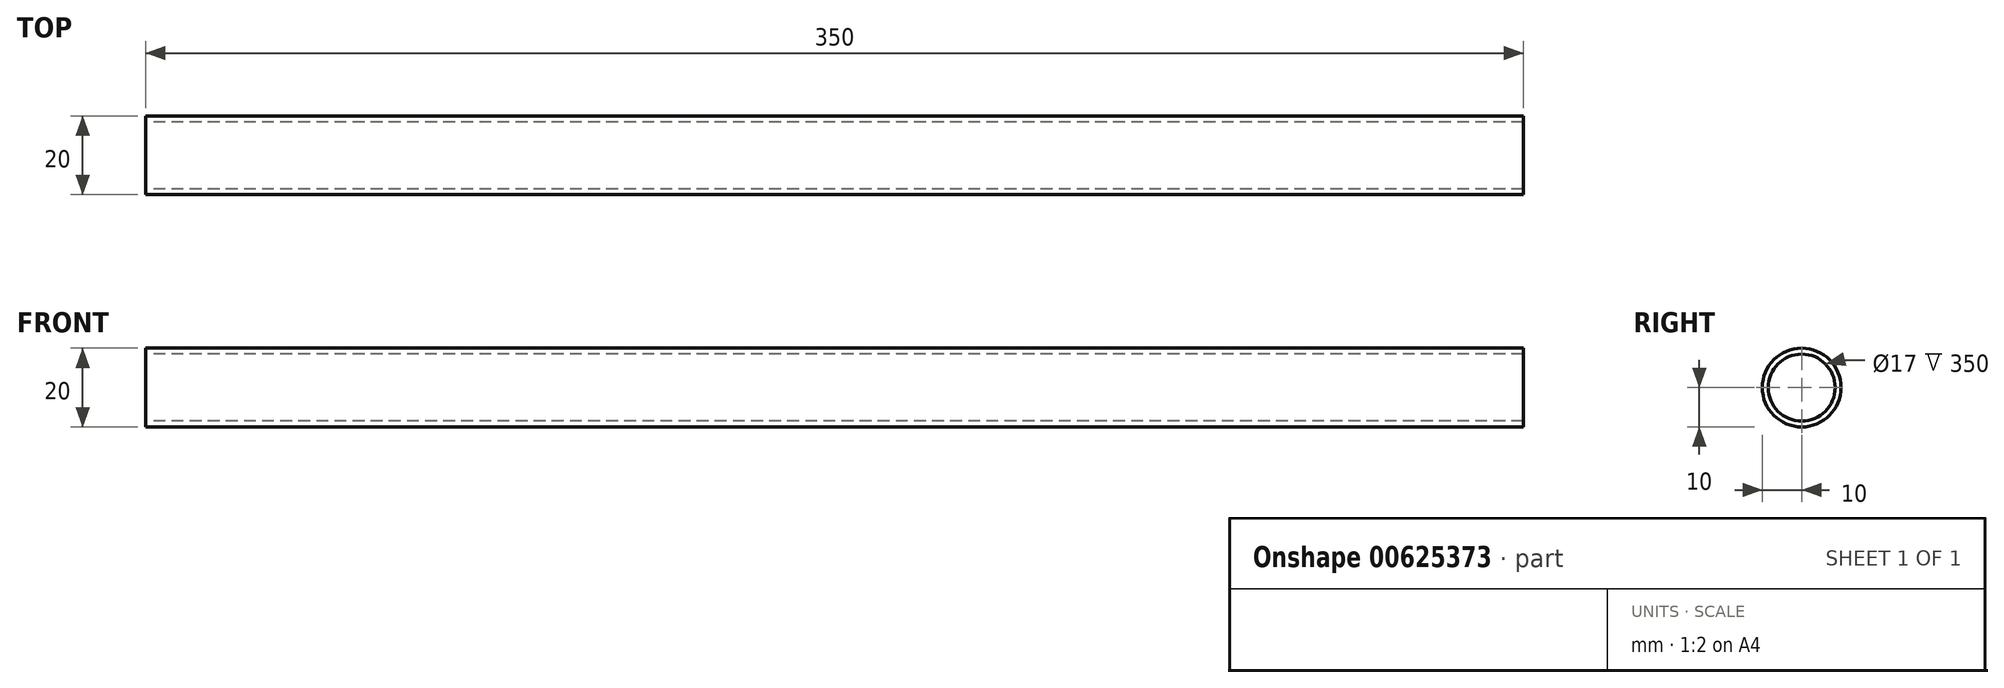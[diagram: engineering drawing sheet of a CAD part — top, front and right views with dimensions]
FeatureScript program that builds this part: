
annotation { "Feature Type Name" : "Feature", "Feature Type Description" : "" }
export const myFeature = defineFeature(function(context is Context, id is Id, definition is map)
    precondition{}
    {
        {
            var Q0;
            Q0=qCreatedBy(makeId("Top.planeOp"),FACE);
            var sketch = newSketch(context, id + "F0", { "sketchPlane" : qUnion([Q0])});
            skLineSegment(sketch, "E0.bottom", {"start": v(175, 10) * mm, "end": v(-175, 10) * mm});
            skLineSegment(sketch, "E0.top", {"start": v(175, -10) * mm, "end": v(-175, -10) * mm});
            skLineSegment(sketch, "E0.left", {"start": v(175, 10) * mm, "end": v(175, -10) * mm});
            skLineSegment(sketch, "E0.right", {"start": v(-175, 10) * mm, "end": v(-175, -10) * mm});
            skPoint(sketch, "E0.middle", {"position": v(0, 0) * mm});
            skSolve(sketch);
        }
        {
            var Q0;
            Q0=makeQuery(id+"F0.imprint","IMPRINT",FACE,{"disambiguationData":[TD([[makeQuery(id+"F0.imprint","IMPRINT",EDGE,{"derivedFrom":sQuery(id+"F0.wireOp",EDGE,"E0.bottom")}),1.0]])]});
            extrude(context, id + "F1", {"entities" : qUnion([Q0]), "depth" : 10 * mm, "offsetDistance" : 25 * mm, "hasSecondDirection" : true, "secondDirectionOppositeDirection" : true, "secondDirectionDepth" : 10 * mm});
        }
        {
            var Q0;
            Q0=makeQuery(id+"F1.opExtrude","SWEPT_FACE",FACE,{"disambiguationData":[OSD([sQuery(id+"F0.wireOp",EDGE,"E0.right")])]});
            var sketch = newSketch(context, id + "F2", { "sketchPlane" : qUnion([Q0])});
            skCircle(sketch, "E1", {"center": v(0, 0) * mm, "radius": 10 * mm});
            skCircle(sketch, "E2", {"center": v(0, 0) * mm, "radius": 8.5 * mm});
            skSolve(sketch);
        }
        {
            var Q0;
            {var subQ0=sQuery(id+"F2.wireOp",EDGE,"E1");var subQ1=sQuery(id+"F0.wireOp",EDGE,"E0.right");var subQ2=makeQuery(id+"F1.opExtrude","CAP_EDGE",EDGE,{"disambiguationData":[OSD([subQ1])],"isStart":false});var subQ3=makeQuery(id+"F2.imprint","INTERSECT",VERTEX,{"derivedFrom":[subQ2,subQ0]});Q0=makeQuery(id+"F2.imprint","IMPRINT",FACE,{"disambiguationData":[TD([[makeQuery(id+"F2.imprint","IMPRINT",EDGE,{"disambiguationData":[TD([[subQ3,-1.0]])],"derivedFrom":subQ0}),-1.0]])]});}
            var Q1;
            {var subQ0=sQuery(id+"F2.wireOp",EDGE,"E1");var subQ1=sQuery(id+"F0.wireOp",EDGE,"E0.right");var subQ4=makeQuery(id+"F1.opExtrude","CAP_EDGE",EDGE,{"disambiguationData":[OSD([subQ1])],"isStart":true});var subQ5=makeQuery(id+"F2.imprint","INTERSECT",VERTEX,{"derivedFrom":[subQ4,subQ0]});Q1=makeQuery(id+"F2.imprint","IMPRINT",FACE,{"disambiguationData":[TD([[makeQuery(id+"F2.imprint","IMPRINT",EDGE,{"disambiguationData":[TD([[subQ5,1.0]])],"derivedFrom":subQ0}),-1.0]])]});}
            var Q2;
            {var subQ0=sQuery(id+"F2.wireOp",EDGE,"E1");var subQ1=sQuery(id+"F0.wireOp",EDGE,"E0.right");var subQ2=makeQuery(id+"F1.opExtrude","CAP_EDGE",EDGE,{"disambiguationData":[OSD([subQ1])],"isStart":false});var subQ3=makeQuery(id+"F2.imprint","INTERSECT",VERTEX,{"derivedFrom":[subQ2,subQ0]});Q2=makeQuery(id+"F2.imprint","IMPRINT",FACE,{"disambiguationData":[TD([[makeQuery(id+"F2.imprint","IMPRINT",EDGE,{"disambiguationData":[TD([[subQ3,1.0]])],"derivedFrom":subQ0}),-1.0]])]});}
            var Q3;
            {var subQ0=sQuery(id+"F2.wireOp",EDGE,"E1");var subQ1=sQuery(id+"F0.wireOp",EDGE,"E0.right");var subQ4=makeQuery(id+"F1.opExtrude","CAP_EDGE",EDGE,{"disambiguationData":[OSD([subQ1])],"isStart":true});var subQ5=makeQuery(id+"F2.imprint","INTERSECT",VERTEX,{"derivedFrom":[subQ4,subQ0]});Q3=makeQuery(id+"F2.imprint","IMPRINT",FACE,{"disambiguationData":[TD([[makeQuery(id+"F2.imprint","IMPRINT",EDGE,{"disambiguationData":[TD([[subQ5,-1.0]])],"derivedFrom":subQ0}),-1.0]])]});}
            var Q4;
            Q4=makeQuery(id+"F2.imprint","IMPRINT",FACE,{"disambiguationData":[TD([[makeQuery(id+"F2.imprint","IMPRINT",EDGE,{"derivedFrom":sQuery(id+"F2.wireOp",EDGE,"E2")}),1.0]])]});
            extrude(context, id + "F3", {"entities" : qUnion([Q0, Q1, Q2, Q3, Q4]), "operationType" : NewBodyOperationType.REMOVE, "oppositeDirection" : true, "depth" : 355.6 * mm, "offsetDistance" : 25 * mm});
        }
        {
            var Q0;
            Q0=qCreatedBy(makeId("Top.planeOp"),FACE);
            cPlane(context, id + "F4", {"entities" : qUnion([Q0]), "cplaneType" : CPlaneType.OFFSET, "offset" : (3 / 4) / 50.8 * mm, "width" : 150 * mm, "height" : 150 * mm});
        }
    });
